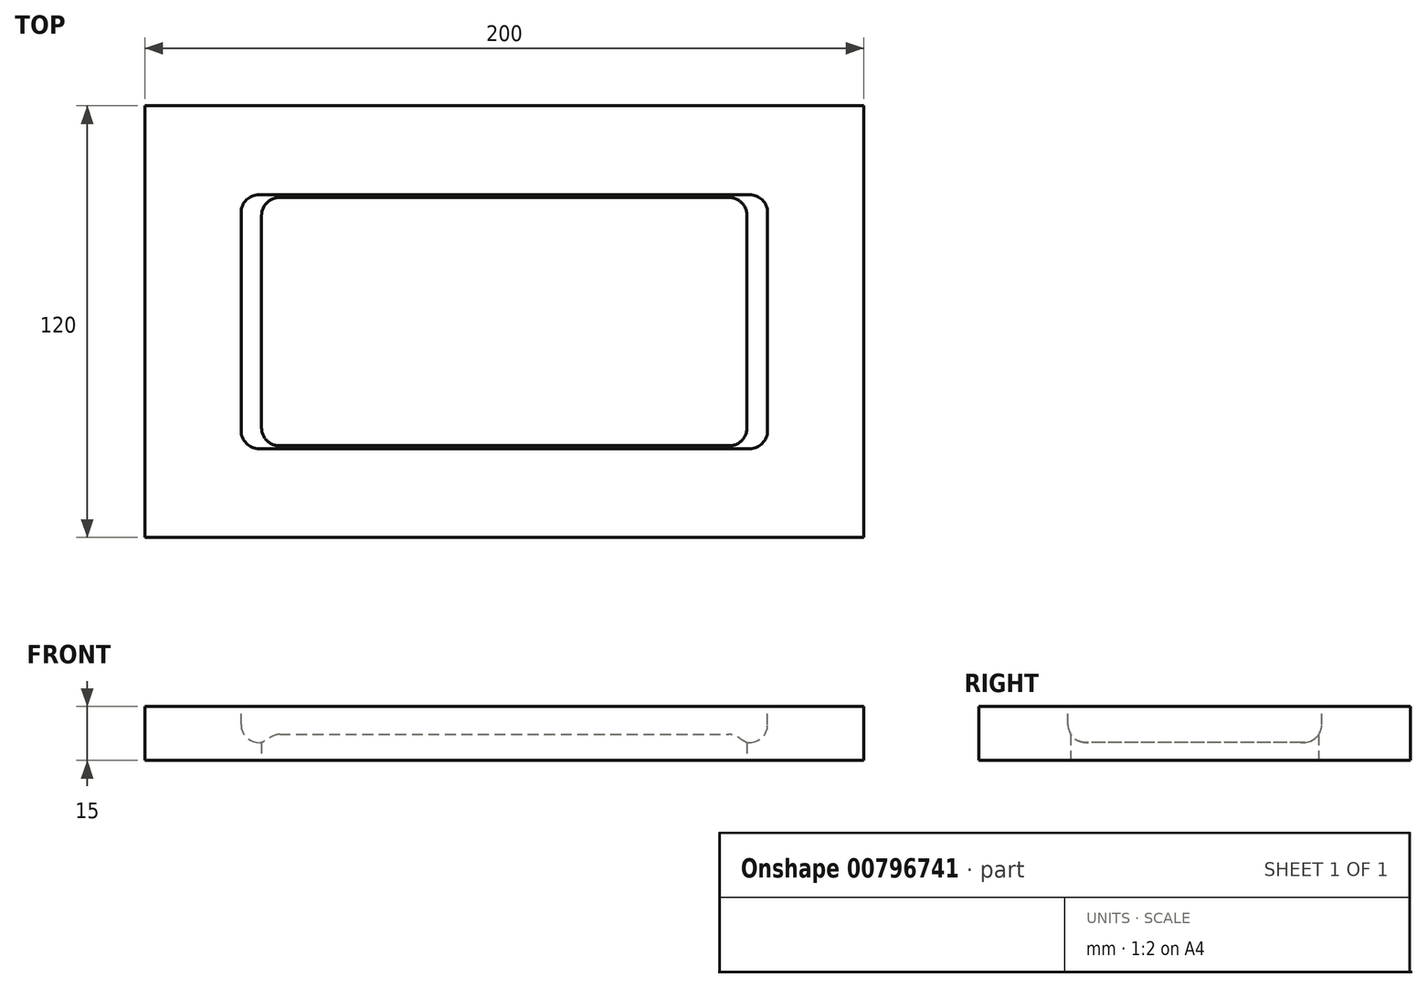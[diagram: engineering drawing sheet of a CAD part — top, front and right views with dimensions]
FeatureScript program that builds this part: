
annotation { "Feature Type Name" : "Feature", "Feature Type Description" : "" }
export const myFeature = defineFeature(function(context is Context, id is Id, definition is map)
    precondition{}
    {
        {
            var Q0;
            Q0=qCreatedBy(makeId("Top.planeOp"),FACE);
            var sketch = newSketch(context, id + "F0", { "sketchPlane" : qUnion([Q0])});
            skLineSegment(sketch, "E0.bottom", {"start": v(-100, 60) * mm, "end": v(100, 60) * mm});
            skLineSegment(sketch, "E0.top", {"start": v(-100, -60) * mm, "end": v(100, -60) * mm});
            skLineSegment(sketch, "E0.left", {"start": v(-100, 60) * mm, "end": v(-100, -60) * mm});
            skLineSegment(sketch, "E0.right", {"start": v(100, 60) * mm, "end": v(100, -60) * mm});
            skSolve(sketch);
        }
        {
            var Q0;
            Q0=makeQuery(id+"F0.imprint","IMPRINT",FACE,{"disambiguationData":[TD([[makeQuery(id+"F0.imprint","IMPRINT",EDGE,{"derivedFrom":sQuery(id+"F0.wireOp",EDGE,"E0.bottom")}),-1.0]])]});
            extrude(context, id + "F1", {"entities" : qUnion([Q0]), "depth" : 15 * mm, "offsetDistance" : 25 * mm});
        }
        {
            var Q0;
            Q0=makeQuery(id+"F1.opExtrude","CAP_FACE",FACE,{"disambiguationData":[OSD([sQuery(id+"F0.wireOp",EDGE,"E0.bottom"),sQuery(id+"F0.wireOp",EDGE,"E0.top"),sQuery(id+"F0.wireOp",EDGE,"E0.left"),sQuery(id+"F0.wireOp",EDGE,"E0.right")])],"isStart":false});
            var sketch = newSketch(context, id + "F2", { "sketchPlane" : qUnion([Q0])});
            skLineSegment(sketch, "E1.bottom", {"start": v(-73.2, 35.3) * mm, "end": v(73.2, 35.3) * mm});
            skLineSegment(sketch, "E1.top", {"start": v(-73.2, -35.3) * mm, "end": v(73.2, -35.3) * mm});
            skLineSegment(sketch, "E1.left", {"start": v(-73.2, 35.3) * mm, "end": v(-73.2, -35.3) * mm});
            skLineSegment(sketch, "E1.right", {"start": v(73.2, 35.3) * mm, "end": v(73.2, -35.3) * mm});
            skSolve(sketch);
        }
        {
            var Q0;
            Q0=makeQuery(id+"F2.imprint","IMPRINT",FACE,{"disambiguationData":[TD([[makeQuery(id+"F2.imprint","IMPRINT",EDGE,{"derivedFrom":sQuery(id+"F2.wireOp",EDGE,"E1.bottom")}),-1.0]])]});
            extrude(context, id + "F3", {"entities" : qUnion([Q0]), "operationType" : NewBodyOperationType.REMOVE, "oppositeDirection" : true, "depth" : 10 * mm, "offsetDistance" : 25 * mm});
        }
        {
            var Q0;
            Q0=makeQuery(id+"F3.boolean.opBoolean","COPY",EDGE,{"derivedFrom":makeQuery(id+"F3.opExtrude","SWEPT_EDGE",EDGE,{"disambiguationData":[OSD([sQuery(id+"F2.wireOp",EDGE,"E1.bottom"),sQuery(id+"F2.wireOp",EDGE,"E1.left")])]})});
            fillet(context, id + "F4", {"entities" : qUnion([Q0]), "radius" : 5 * mm, "tangentPropagation" : true, "allowEdgeOverflow" : false});
        }
        {
            var Q0;
            Q0=makeQuery(id+"F3.boolean.opBoolean","COPY",EDGE,{"derivedFrom":makeQuery(id+"F3.opExtrude","SWEPT_EDGE",EDGE,{"disambiguationData":[OSD([sQuery(id+"F2.wireOp",EDGE,"E1.top"),sQuery(id+"F2.wireOp",EDGE,"E1.left")])]})});
            fillet(context, id + "F5", {"entities" : qUnion([Q0]), "radius" : 5 * mm, "tangentPropagation" : true, "allowEdgeOverflow" : false});
        }
        {
            var Q0;
            Q0=makeQuery(id+"F3.boolean.opBoolean","COPY",EDGE,{"derivedFrom":makeQuery(id+"F3.opExtrude","SWEPT_EDGE",EDGE,{"disambiguationData":[OSD([sQuery(id+"F2.wireOp",EDGE,"E1.top"),sQuery(id+"F2.wireOp",EDGE,"E1.right")])]})});
            fillet(context, id + "F6", {"entities" : qUnion([Q0]), "radius" : 5 * mm, "tangentPropagation" : true, "allowEdgeOverflow" : false});
        }
        {
            var Q0;
            Q0=makeQuery(id+"F3.boolean.opBoolean","COPY",EDGE,{"derivedFrom":makeQuery(id+"F3.opExtrude","SWEPT_EDGE",EDGE,{"disambiguationData":[OSD([sQuery(id+"F2.wireOp",EDGE,"E1.bottom"),sQuery(id+"F2.wireOp",EDGE,"E1.right")])]})});
            fillet(context, id + "F7", {"entities" : qUnion([Q0]), "radius" : 5 * mm, "tangentPropagation" : true, "allowEdgeOverflow" : false});
        }
        {
            var Q0;
            Q0=makeQuery(id+"F3.boolean.opBoolean","COPY",EDGE,{"derivedFrom":makeQuery(id+"F3.opExtrude","CAP_EDGE",EDGE,{"disambiguationData":[OSD([sQuery(id+"F2.wireOp",EDGE,"E1.right")])],"isStart":false})});
            var Q1;
            Q1=makeQuery(id+"F3.boolean.opBoolean","COPY",EDGE,{"derivedFrom":makeQuery(id+"F3.opExtrude","CAP_EDGE",EDGE,{"disambiguationData":[OSD([sQuery(id+"F2.wireOp",EDGE,"E1.bottom")])],"isStart":false})});
            var Q2;
            Q2=makeQuery(id+"F3.boolean.opBoolean","COPY",EDGE,{"derivedFrom":makeQuery(id+"F3.opExtrude","CAP_EDGE",EDGE,{"disambiguationData":[OSD([sQuery(id+"F2.wireOp",EDGE,"E1.top")])],"isStart":false})});
            var Q3;
            Q3=makeQuery(id+"F3.boolean.opBoolean","COPY",EDGE,{"derivedFrom":makeQuery(id+"F3.opExtrude","CAP_EDGE",EDGE,{"disambiguationData":[OSD([sQuery(id+"F2.wireOp",EDGE,"E1.left")])],"isStart":false})});
            fillet(context, id + "F8", {"entities" : qUnion([Q0, Q1, Q2, Q3]), "radius" : 5 * mm, "tangentPropagation" : true, "allowEdgeOverflow" : false});
        }
        {
            var Q0;
            Q0=makeQuery(id+"F1.opExtrude","CAP_FACE",FACE,{"disambiguationData":[OSD([sQuery(id+"F0.wireOp",EDGE,"E0.bottom"),sQuery(id+"F0.wireOp",EDGE,"E0.top"),sQuery(id+"F0.wireOp",EDGE,"E0.left"),sQuery(id+"F0.wireOp",EDGE,"E0.right")])],"isStart":true});
            var sketch = newSketch(context, id + "F9", { "sketchPlane" : qUnion([Q0])});
            skLineSegment(sketch, "E2.bottom", {"start": v(-67.5, 34.5) * mm, "end": v(67.5, 34.5) * mm});
            skLineSegment(sketch, "E2.top", {"start": v(-67.5, -34.5) * mm, "end": v(67.5, -34.5) * mm});
            skLineSegment(sketch, "E2.left", {"start": v(-67.5, 34.5) * mm, "end": v(-67.5, -34.5) * mm});
            skLineSegment(sketch, "E2.right", {"start": v(67.5, 34.5) * mm, "end": v(67.5, -34.5) * mm});
            skSolve(sketch);
        }
        {
            var Q0;
            Q0=makeQuery(id+"F9.imprint","IMPRINT",FACE,{"disambiguationData":[TD([[makeQuery(id+"F9.imprint","IMPRINT",EDGE,{"derivedFrom":sQuery(id+"F9.wireOp",EDGE,"E2.bottom")}),-1.0]])]});
            extrude(context, id + "F10", {"entities" : qUnion([Q0]), "operationType" : NewBodyOperationType.REMOVE, "oppositeDirection" : true, "depth" : 25 * mm, "offsetDistance" : 25 * mm});
        }
        {
            var Q0;
            Q0=makeQuery(id+"F10.boolean.opBoolean","COPY",EDGE,{"derivedFrom":makeQuery(id+"F10.opExtrude","SWEPT_EDGE",EDGE,{"disambiguationData":[OSD([sQuery(id+"F9.wireOp",EDGE,"E2.bottom"),sQuery(id+"F9.wireOp",EDGE,"E2.right")])]})});
            fillet(context, id + "F11", {"entities" : qUnion([Q0]), "radius" : 5 * mm, "tangentPropagation" : true, "allowEdgeOverflow" : false});
        }
        {
            var Q0;
            Q0=makeQuery(id+"F10.boolean.opBoolean","COPY",EDGE,{"derivedFrom":makeQuery(id+"F10.opExtrude","SWEPT_EDGE",EDGE,{"disambiguationData":[OSD([sQuery(id+"F9.wireOp",EDGE,"E2.top"),sQuery(id+"F9.wireOp",EDGE,"E2.right")])]})});
            fillet(context, id + "F12", {"entities" : qUnion([Q0]), "radius" : 5 * mm, "tangentPropagation" : true, "allowEdgeOverflow" : false});
        }
        {
            var Q0;
            Q0=makeQuery(id+"F10.boolean.opBoolean","COPY",EDGE,{"derivedFrom":makeQuery(id+"F10.opExtrude","SWEPT_EDGE",EDGE,{"disambiguationData":[OSD([sQuery(id+"F9.wireOp",EDGE,"E2.top"),sQuery(id+"F9.wireOp",EDGE,"E2.left")])]})});
            fillet(context, id + "F13", {"entities" : qUnion([Q0]), "radius" : 5 * mm, "tangentPropagation" : true, "allowEdgeOverflow" : false});
        }
        {
            var Q0;
            Q0=makeQuery(id+"F10.boolean.opBoolean","COPY",EDGE,{"derivedFrom":makeQuery(id+"F10.opExtrude","SWEPT_EDGE",EDGE,{"disambiguationData":[OSD([sQuery(id+"F9.wireOp",EDGE,"E2.bottom"),sQuery(id+"F9.wireOp",EDGE,"E2.left")])]})});
            fillet(context, id + "F14", {"entities" : qUnion([Q0]), "radius" : 5 * mm, "tangentPropagation" : true, "allowEdgeOverflow" : false});
        }
    });
